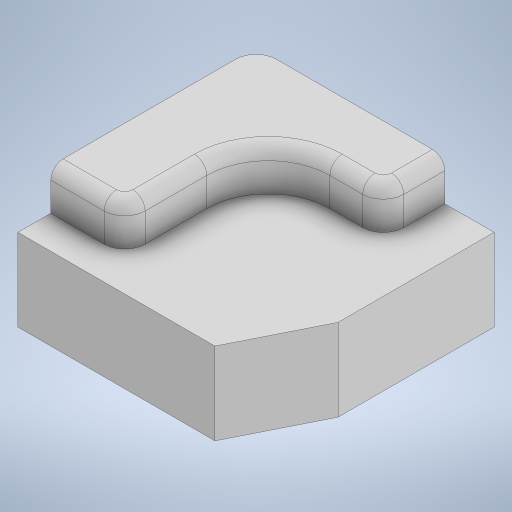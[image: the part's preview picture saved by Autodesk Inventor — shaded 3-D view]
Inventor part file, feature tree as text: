
AUTODESK INVENTOR PART (.ipt)
format: ipt  version: 2023 (Build 270158000, 158)  size: 248,832 bytes
history: native  units: mm
features: extrude x2, fillet x2, sketch x1
ambient origin geometry x8: Origin, YZ Plane, XZ Plane, XY Plane, X Axis, Y Axis, Z Axis, Center Point
bodies: Body1 (feature_tree)
feature tree (5):
  sketch  "Schizzo11"
  extrude  "Estrusione6"  Depth=58.0mm
  extrude  "Estrusione7"  Depth=58.0mm
  fillet  "Raccordo3"  Radius=50.0mm
  fillet  "Raccordo4"  Radius=18.0mm
